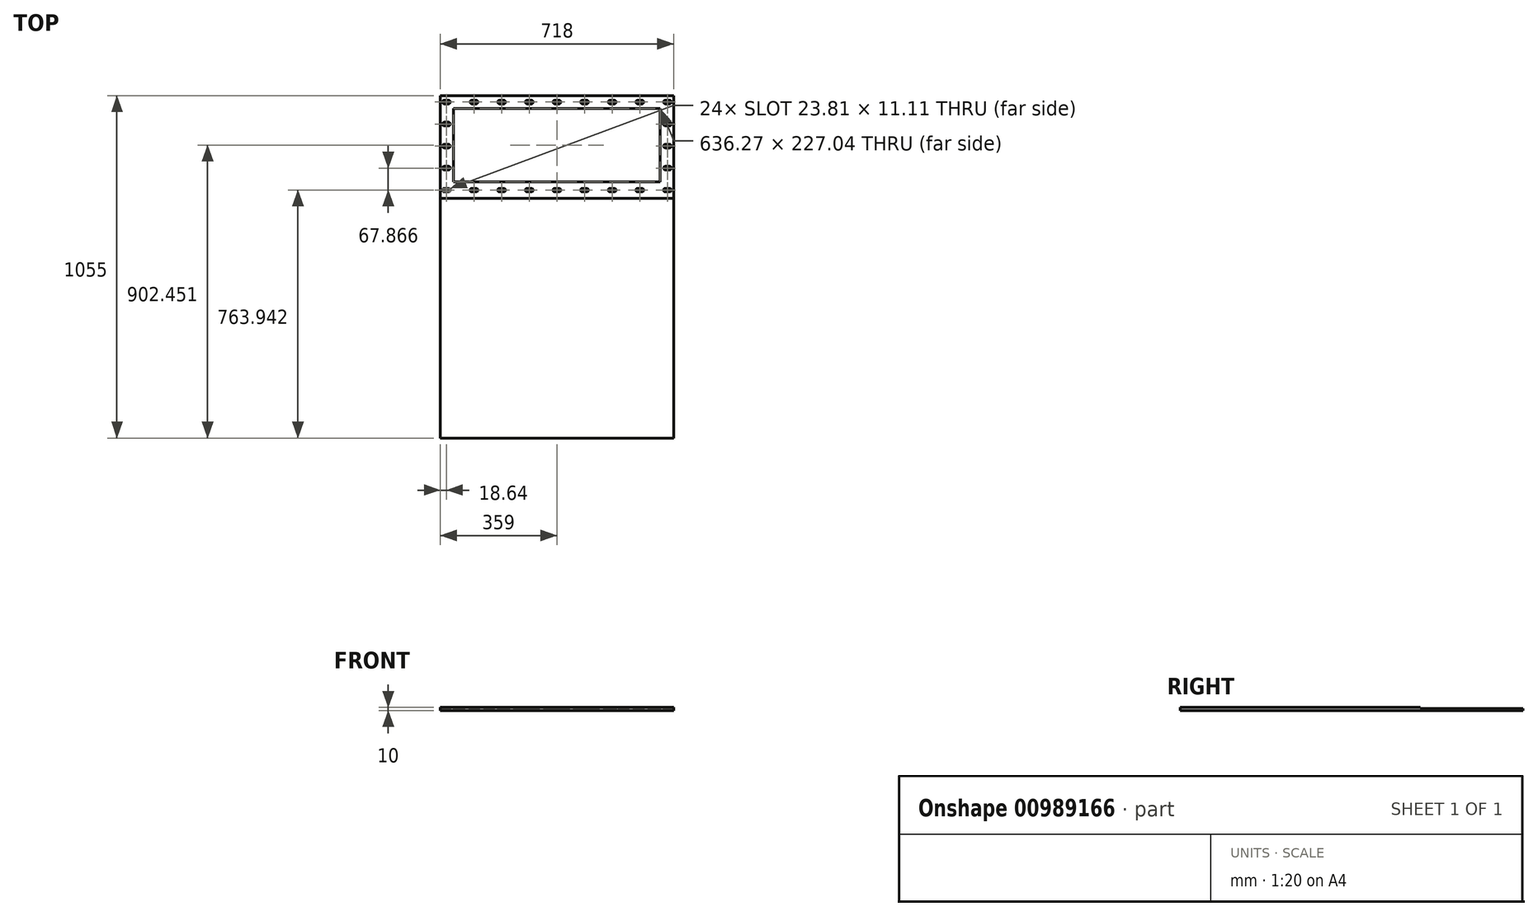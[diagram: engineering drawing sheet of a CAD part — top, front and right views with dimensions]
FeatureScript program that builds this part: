
annotation { "Feature Type Name" : "Feature", "Feature Type Description" : "" }
export const myFeature = defineFeature(function(context is Context, id is Id, definition is map)
    precondition{}
    {
        {
            var Q0;
            Q0=qCreatedBy(makeId("Top.planeOp"),FACE);
            var sketch = newSketch(context, id + "F0", { "sketchPlane" : qUnion([Q0])});
            skLineSegment(sketch, "E0.bottom", {"start": v(0, 0) * mm, "end": v(718, 0) * mm});
            skLineSegment(sketch, "E0.top", {"start": v(0, 1055) * mm, "end": v(718, 1055) * mm});
            skLineSegment(sketch, "E0.right", {"start": v(718, 0) * mm, "end": v(718, 1055) * mm});
            skLineSegment(sketch, "E1", {"start": v(352.65, 769.5) * mm, "end": v(365.35, 769.5) * mm});
            skLineSegment(sketch, "E2", {"start": v(352.65, 758.39) * mm, "end": v(365.35, 758.39) * mm});
            skArc(sketch, "E3", {"start": v(365.35, 758.39) * mm, "mid": v(370.9, 763.94) * mm, "end": v(365.35, 769.5) * mm});
            skArc(sketch, "E4", {"start": v(352.65, 769.5) * mm, "mid": v(347.1, 763.94) * mm, "end": v(352.65, 758.39) * mm});
            skPoint(sketch, "E5.center.orphan", {"position": v(359, 763.94) * mm});
            skArc(sketch, "E6.MirrorCS", {"start": v(450.44, 769.5) * mm, "mid": v(456, 763.94) * mm, "end": v(450.44, 758.39) * mm});
            skArc(sketch, "E7.MirrorCS", {"start": v(437.74, 758.39) * mm, "mid": v(432.18, 763.94) * mm, "end": v(437.74, 769.5) * mm});
            skLineSegment(sketch, "E8.MirrorCS", {"start": v(450.44, 758.39) * mm, "end": v(437.74, 758.39) * mm});
            skLineSegment(sketch, "E9.MirrorCS", {"start": v(450.44, 769.5) * mm, "end": v(437.74, 769.5) * mm});
            skPoint(sketch, "E10.MirrorP", {"position": v(444.09, 763.94) * mm});
            skPoint(sketch, "E11.MirrorP", {"position": v(529.18, 763.94) * mm});
            skLineSegment(sketch, "E12.MirrorCS", {"start": v(522.83, 758.39) * mm, "end": v(535.53, 758.39) * mm});
            skPoint(sketch, "E13.MirrorP", {"position": v(614.27, 763.94) * mm});
            skArc(sketch, "E14.MirrorCS", {"start": v(607.92, 758.39) * mm, "mid": v(602.36, 763.94) * mm, "end": v(607.92, 769.5) * mm});
            skLineSegment(sketch, "E15.MirrorCS", {"start": v(620.62, 758.39) * mm, "end": v(607.92, 758.39) * mm});
            skArc(sketch, "E16.MirrorCS", {"start": v(535.53, 758.39) * mm, "mid": v(541.09, 763.94) * mm, "end": v(535.53, 769.5) * mm});
            skLineSegment(sketch, "E17.MirrorCS", {"start": v(620.62, 769.5) * mm, "end": v(607.92, 769.5) * mm});
            skLineSegment(sketch, "E18.MirrorCS", {"start": v(522.83, 769.5) * mm, "end": v(535.53, 769.5) * mm});
            skArc(sketch, "E19.MirrorCS", {"start": v(620.62, 769.5) * mm, "mid": v(626.18, 763.94) * mm, "end": v(620.62, 758.39) * mm});
            skArc(sketch, "E20.MirrorCS", {"start": v(522.83, 769.5) * mm, "mid": v(517.27, 763.94) * mm, "end": v(522.83, 758.39) * mm});
            skLineSegment(sketch, "E21.MirrorCS", {"start": v(693, 758.39) * mm, "end": v(705.7, 758.39) * mm});
            skPoint(sketch, "E22.MirrorP", {"position": v(699.36, 763.94) * mm});
            skArc(sketch, "E23.MirrorCS", {"start": v(705.7, 758.39) * mm, "mid": v(711.27, 763.94) * mm, "end": v(705.7, 769.5) * mm});
            skLineSegment(sketch, "E24.MirrorCS", {"start": v(693, 769.5) * mm, "end": v(705.7, 769.5) * mm});
            skArc(sketch, "E25.MirrorCS", {"start": v(693, 769.5) * mm, "mid": v(687.45, 763.94) * mm, "end": v(693, 758.39) * mm});
            skArc(sketch, "E26.MirrorCS", {"start": v(24.99, 769.5) * mm, "mid": v(30.55, 763.94) * mm, "end": v(24.99, 758.39) * mm});
            skArc(sketch, "E27.MirrorCS", {"start": v(182.47, 758.39) * mm, "mid": v(176.91, 763.94) * mm, "end": v(182.47, 769.5) * mm});
            skLineSegment(sketch, "E28.MirrorCS", {"start": v(267.56, 769.5) * mm, "end": v(280.26, 769.5) * mm});
            skArc(sketch, "E29.MirrorCS", {"start": v(12.29, 758.39) * mm, "mid": v(6.73, 763.94) * mm, "end": v(12.29, 769.5) * mm});
            skLineSegment(sketch, "E30.MirrorCS", {"start": v(24.99, 758.39) * mm, "end": v(12.29, 758.39) * mm});
            skLineSegment(sketch, "E31.MirrorCS", {"start": v(195.17, 769.5) * mm, "end": v(182.47, 769.5) * mm});
            skLineSegment(sketch, "E32.MirrorCS", {"start": v(97.38, 769.5) * mm, "end": v(110.08, 769.5) * mm});
            skPoint(sketch, "E33.MirrorP", {"position": v(273.9, 763.94) * mm});
            skArc(sketch, "E34.MirrorCS", {"start": v(280.26, 758.39) * mm, "mid": v(285.82, 763.94) * mm, "end": v(280.26, 769.5) * mm});
            skArc(sketch, "E35.MirrorCS", {"start": v(267.56, 769.5) * mm, "mid": v(262, 763.94) * mm, "end": v(267.56, 758.39) * mm});
            skLineSegment(sketch, "E36.MirrorCS", {"start": v(267.56, 758.39) * mm, "end": v(280.26, 758.39) * mm});
            skLineSegment(sketch, "E37.MirrorCS", {"start": v(97.38, 758.39) * mm, "end": v(110.08, 758.39) * mm});
            skPoint(sketch, "E38.MirrorP", {"position": v(188.82, 763.94) * mm});
            skArc(sketch, "E39.MirrorCS", {"start": v(195.17, 769.5) * mm, "mid": v(200.73, 763.94) * mm, "end": v(195.17, 758.39) * mm});
            skLineSegment(sketch, "E40.MirrorCS", {"start": v(24.99, 769.5) * mm, "end": v(12.29, 769.5) * mm});
            skLineSegment(sketch, "E41.MirrorCS", {"start": v(195.17, 758.39) * mm, "end": v(182.47, 758.39) * mm});
            skPoint(sketch, "E42.MirrorP", {"position": v(103.73, 763.94) * mm});
            skPoint(sketch, "E43.MirrorP", {"position": v(18.64, 763.94) * mm});
            skArc(sketch, "E44.MirrorCS", {"start": v(97.38, 769.5) * mm, "mid": v(91.82, 763.94) * mm, "end": v(97.38, 758.39) * mm});
            skArc(sketch, "E45.MirrorCS", {"start": v(110.08, 758.39) * mm, "mid": v(115.64, 763.94) * mm, "end": v(110.08, 769.5) * mm});
            skArc(sketch, "E46.MirrorCS", {"start": v(450.44, 1029.85) * mm, "mid": v(456, 1035.4) * mm, "end": v(450.44, 1040.96) * mm});
            skArc(sketch, "E47.MirrorCS", {"start": v(607.92, 1040.96) * mm, "mid": v(602.36, 1035.4) * mm, "end": v(607.92, 1029.85) * mm});
            skArc(sketch, "E48.MirrorCS", {"start": v(522.83, 1029.85) * mm, "mid": v(517.27, 1035.4) * mm, "end": v(522.83, 1040.96) * mm});
            skLineSegment(sketch, "E49.MirrorCS", {"start": v(522.83, 1040.96) * mm, "end": v(535.53, 1040.96) * mm});
            skLineSegment(sketch, "E50.MirrorCS", {"start": v(450.44, 1029.85) * mm, "end": v(437.74, 1029.85) * mm});
            skArc(sketch, "E51.MirrorCS", {"start": v(620.62, 1029.85) * mm, "mid": v(626.18, 1035.4) * mm, "end": v(620.62, 1040.96) * mm});
            skArc(sketch, "E52.MirrorCS", {"start": v(110.08, 1040.96) * mm, "mid": v(115.64, 1035.4) * mm, "end": v(110.08, 1029.85) * mm});
            skLineSegment(sketch, "E53.MirrorCS", {"start": v(620.62, 1029.85) * mm, "end": v(607.92, 1029.85) * mm});
            skArc(sketch, "E54.MirrorCS", {"start": v(437.74, 1040.96) * mm, "mid": v(432.18, 1035.4) * mm, "end": v(437.74, 1029.85) * mm});
            skArc(sketch, "E55.MirrorCS", {"start": v(535.53, 1040.96) * mm, "mid": v(541.09, 1035.4) * mm, "end": v(535.53, 1029.85) * mm});
            skArc(sketch, "E56.MirrorCS", {"start": v(352.65, 1029.85) * mm, "mid": v(347.1, 1035.4) * mm, "end": v(352.65, 1040.96) * mm});
            skLineSegment(sketch, "E57.MirrorCS", {"start": v(450.44, 1040.96) * mm, "end": v(437.74, 1040.96) * mm});
            skLineSegment(sketch, "E58.MirrorCS", {"start": v(620.62, 1040.96) * mm, "end": v(607.92, 1040.96) * mm});
            skLineSegment(sketch, "E59.MirrorCS", {"start": v(522.83, 1029.85) * mm, "end": v(535.53, 1029.85) * mm});
            skLineSegment(sketch, "E60.MirrorCS", {"start": v(693, 1029.85) * mm, "end": v(705.7, 1029.85) * mm});
            skArc(sketch, "E61.MirrorCS", {"start": v(12.29, 1040.96) * mm, "mid": v(6.73, 1035.4) * mm, "end": v(12.29, 1029.85) * mm});
            skLineSegment(sketch, "E62.MirrorCS", {"start": v(693, 1040.96) * mm, "end": v(705.7, 1040.96) * mm});
            skArc(sketch, "E63.MirrorCS", {"start": v(693, 1029.85) * mm, "mid": v(687.45, 1035.4) * mm, "end": v(693, 1040.96) * mm});
            skArc(sketch, "E64.MirrorCS", {"start": v(705.7, 1040.96) * mm, "mid": v(711.27, 1035.4) * mm, "end": v(705.7, 1029.85) * mm});
            skLineSegment(sketch, "E65.MirrorCS", {"start": v(267.56, 1040.96) * mm, "end": v(280.26, 1040.96) * mm});
            skArc(sketch, "E66.MirrorCS", {"start": v(195.17, 1029.85) * mm, "mid": v(200.73, 1035.4) * mm, "end": v(195.17, 1040.96) * mm});
            skLineSegment(sketch, "E67.MirrorCS", {"start": v(195.17, 1029.85) * mm, "end": v(182.47, 1029.85) * mm});
            skLineSegment(sketch, "E68.MirrorCS", {"start": v(195.17, 1040.96) * mm, "end": v(182.47, 1040.96) * mm});
            skLineSegment(sketch, "E69.MirrorCS", {"start": v(24.99, 1029.85) * mm, "end": v(12.29, 1029.85) * mm});
            skArc(sketch, "E70.MirrorCS", {"start": v(267.56, 1029.85) * mm, "mid": v(262, 1035.4) * mm, "end": v(267.56, 1040.96) * mm});
            skLineSegment(sketch, "E71.MirrorCS", {"start": v(352.65, 1029.85) * mm, "end": v(365.35, 1029.85) * mm});
            skLineSegment(sketch, "E72.MirrorCS", {"start": v(352.65, 1040.96) * mm, "end": v(365.35, 1040.96) * mm});
            skArc(sketch, "E73.MirrorCS", {"start": v(24.99, 1029.85) * mm, "mid": v(30.55, 1035.4) * mm, "end": v(24.99, 1040.96) * mm});
            skLineSegment(sketch, "E74.MirrorCS", {"start": v(97.38, 1029.85) * mm, "end": v(110.08, 1029.85) * mm});
            skArc(sketch, "E75.MirrorCS", {"start": v(280.26, 1040.96) * mm, "mid": v(285.82, 1035.4) * mm, "end": v(280.26, 1029.85) * mm});
            skArc(sketch, "E76.MirrorCS", {"start": v(97.38, 1029.85) * mm, "mid": v(91.82, 1035.4) * mm, "end": v(97.38, 1040.96) * mm});
            skArc(sketch, "E77.MirrorCS", {"start": v(182.47, 1040.96) * mm, "mid": v(176.91, 1035.4) * mm, "end": v(182.47, 1029.85) * mm});
            skLineSegment(sketch, "E78.MirrorCS", {"start": v(97.38, 1040.96) * mm, "end": v(110.08, 1040.96) * mm});
            skArc(sketch, "E79.MirrorCS", {"start": v(365.35, 1040.96) * mm, "mid": v(370.9, 1035.4) * mm, "end": v(365.35, 1029.85) * mm});
            skLineSegment(sketch, "E80.MirrorCS", {"start": v(267.56, 1029.85) * mm, "end": v(280.26, 1029.85) * mm});
            skLineSegment(sketch, "E81.MirrorCS", {"start": v(24.99, 1040.96) * mm, "end": v(12.29, 1040.96) * mm});
            skPoint(sketch, "E82.MirrorP", {"position": v(18.64, 1035.4) * mm});
            skPoint(sketch, "E83.MirrorP", {"position": v(359, 1035.4) * mm});
            skPoint(sketch, "E84.MirrorP", {"position": v(699.36, 1035.4) * mm});
            skPoint(sketch, "E85.MirrorP", {"position": v(273.9, 1035.4) * mm});
            skPoint(sketch, "E86.MirrorP", {"position": v(444.09, 1035.4) * mm});
            skPoint(sketch, "E87.MirrorP", {"position": v(103.73, 1035.4) * mm});
            skPoint(sketch, "E88.MirrorP", {"position": v(529.18, 1035.4) * mm});
            skPoint(sketch, "E89.MirrorP", {"position": v(614.27, 1035.4) * mm});
            skPoint(sketch, "E90.MirrorP", {"position": v(188.82, 1035.4) * mm});
            skPoint(sketch, "E91.MirrorP", {"position": v(18.64, 899.67) * mm});
            skLineSegment(sketch, "E92.MirrorCS", {"start": v(24.99, 905.23) * mm, "end": v(12.29, 905.23) * mm});
            skLineSegment(sketch, "E93.MirrorCS", {"start": v(24.99, 894.12) * mm, "end": v(12.29, 894.12) * mm});
            skArc(sketch, "E94.MirrorCS", {"start": v(12.29, 905.23) * mm, "mid": v(6.73, 899.67) * mm, "end": v(12.29, 894.12) * mm});
            skArc(sketch, "E95.MirrorCS", {"start": v(24.99, 894.12) * mm, "mid": v(30.55, 899.67) * mm, "end": v(24.99, 905.23) * mm});
            skArc(sketch, "E96.MirrorCS", {"start": v(24.99, 826.25) * mm, "mid": v(30.55, 831.8) * mm, "end": v(24.99, 837.36) * mm});
            skLineSegment(sketch, "E97.MirrorCS", {"start": v(24.99, 837.36) * mm, "end": v(12.29, 837.36) * mm});
            skLineSegment(sketch, "E98.MirrorCS", {"start": v(24.99, 826.25) * mm, "end": v(12.29, 826.25) * mm});
            skPoint(sketch, "E99.MirrorP", {"position": v(18.64, 831.8) * mm});
            skArc(sketch, "E100.MirrorCS", {"start": v(12.29, 837.36) * mm, "mid": v(6.73, 831.8) * mm, "end": v(12.29, 826.25) * mm});
            skLineSegment(sketch, "E101.MirrorCS", {"start": v(24.99, 973.1) * mm, "end": v(12.29, 973.1) * mm});
            skLineSegment(sketch, "E102.MirrorCS", {"start": v(24.99, 961.98) * mm, "end": v(12.29, 961.98) * mm});
            skPoint(sketch, "E103.MirrorP", {"position": v(18.64, 967.54) * mm});
            skArc(sketch, "E104.MirrorCS", {"start": v(24.99, 973.1) * mm, "mid": v(30.55, 967.54) * mm, "end": v(24.99, 961.98) * mm});
            skArc(sketch, "E105.MirrorCS", {"start": v(12.29, 961.98) * mm, "mid": v(6.73, 967.54) * mm, "end": v(12.29, 973.1) * mm});
            skLineSegment(sketch, "E106.MirrorCS", {"start": v(693, 837.36) * mm, "end": v(705.7, 837.36) * mm});
            skLineSegment(sketch, "E107.MirrorCS", {"start": v(693, 905.23) * mm, "end": v(705.7, 905.23) * mm});
            skLineSegment(sketch, "E108.MirrorCS", {"start": v(693, 894.12) * mm, "end": v(705.7, 894.12) * mm});
            skLineSegment(sketch, "E109.MirrorCS", {"start": v(693, 826.25) * mm, "end": v(705.7, 826.25) * mm});
            skArc(sketch, "E110.MirrorCS", {"start": v(705.7, 837.36) * mm, "mid": v(711.27, 831.8) * mm, "end": v(705.7, 826.25) * mm});
            skLineSegment(sketch, "E111.MirrorCS", {"start": v(693, 973.1) * mm, "end": v(705.7, 973.1) * mm});
            skLineSegment(sketch, "E112.MirrorCS", {"start": v(693, 961.98) * mm, "end": v(705.7, 961.98) * mm});
            skArc(sketch, "E113.MirrorCS", {"start": v(693, 826.25) * mm, "mid": v(687.45, 831.8) * mm, "end": v(693, 837.36) * mm});
            skPoint(sketch, "E114.MirrorP", {"position": v(699.36, 831.8) * mm});
            skArc(sketch, "E115.MirrorCS", {"start": v(693, 894.12) * mm, "mid": v(687.45, 899.67) * mm, "end": v(693, 905.23) * mm});
            skArc(sketch, "E116.MirrorCS", {"start": v(705.7, 961.98) * mm, "mid": v(711.27, 967.54) * mm, "end": v(705.7, 973.1) * mm});
            skArc(sketch, "E117.MirrorCS", {"start": v(693, 973.1) * mm, "mid": v(687.45, 967.54) * mm, "end": v(693, 961.98) * mm});
            skPoint(sketch, "E118.MirrorP", {"position": v(699.36, 967.54) * mm});
            skArc(sketch, "E119.MirrorCS", {"start": v(705.7, 905.23) * mm, "mid": v(711.27, 899.67) * mm, "end": v(705.7, 894.12) * mm});
            skPoint(sketch, "E120.MirrorP", {"position": v(699.36, 899.67) * mm});
            skLineSegment(sketch, "E121", {"start": v(0, 0) * mm, "end": v(0, 1055) * mm});
            skLineSegment(sketch, "E122", {"start": v(0, 738.95) * mm, "end": v(718, 738.95) * mm});
            skLineSegment(sketch, "E123.bottom", {"start": v(40.86, 1015.97) * mm, "end": v(677.13, 1015.97) * mm});
            skLineSegment(sketch, "E123.top", {"start": v(40.86, 788.93) * mm, "end": v(677.13, 788.93) * mm});
            skLineSegment(sketch, "E123.left", {"start": v(40.86, 1015.97) * mm, "end": v(40.86, 788.93) * mm});
            skLineSegment(sketch, "E123.right", {"start": v(677.13, 1015.97) * mm, "end": v(677.13, 788.93) * mm});
            skSolve(sketch);
        }
        {
            var Q0;
            {var subQ0=sQuery(id+"F0.wireOp",EDGE,"E0.bottom");Q0=makeQuery(id+"F0.imprint","IMPRINT",FACE,{"disambiguationData":[TD([[makeQuery(id+"F0.imprint","IMPRINT",EDGE,{"derivedFrom":subQ0}),1.0]])]});}
            extrude(context, id + "F1", {"entities" : qUnion([Q0]), "depth" : 10 * mm, "offsetDistance" : 25.4 * mm});
        }
        {
            var Q0;
            {var subQ1=sQuery(id+"F0.wireOp",EDGE,"E0.top");Q0=makeQuery(id+"F0.imprint","IMPRINT",FACE,{"disambiguationData":[TD([[makeQuery(id+"F0.imprint","IMPRINT",EDGE,{"derivedFrom":subQ1}),-1.0]])]});}
            extrude(context, id + "F2", {"entities" : qUnion([Q0]), "operationType" : NewBodyOperationType.ADD, "depth" : 6.9 * mm, "offsetDistance" : 25.4 * mm});
        }
    });
